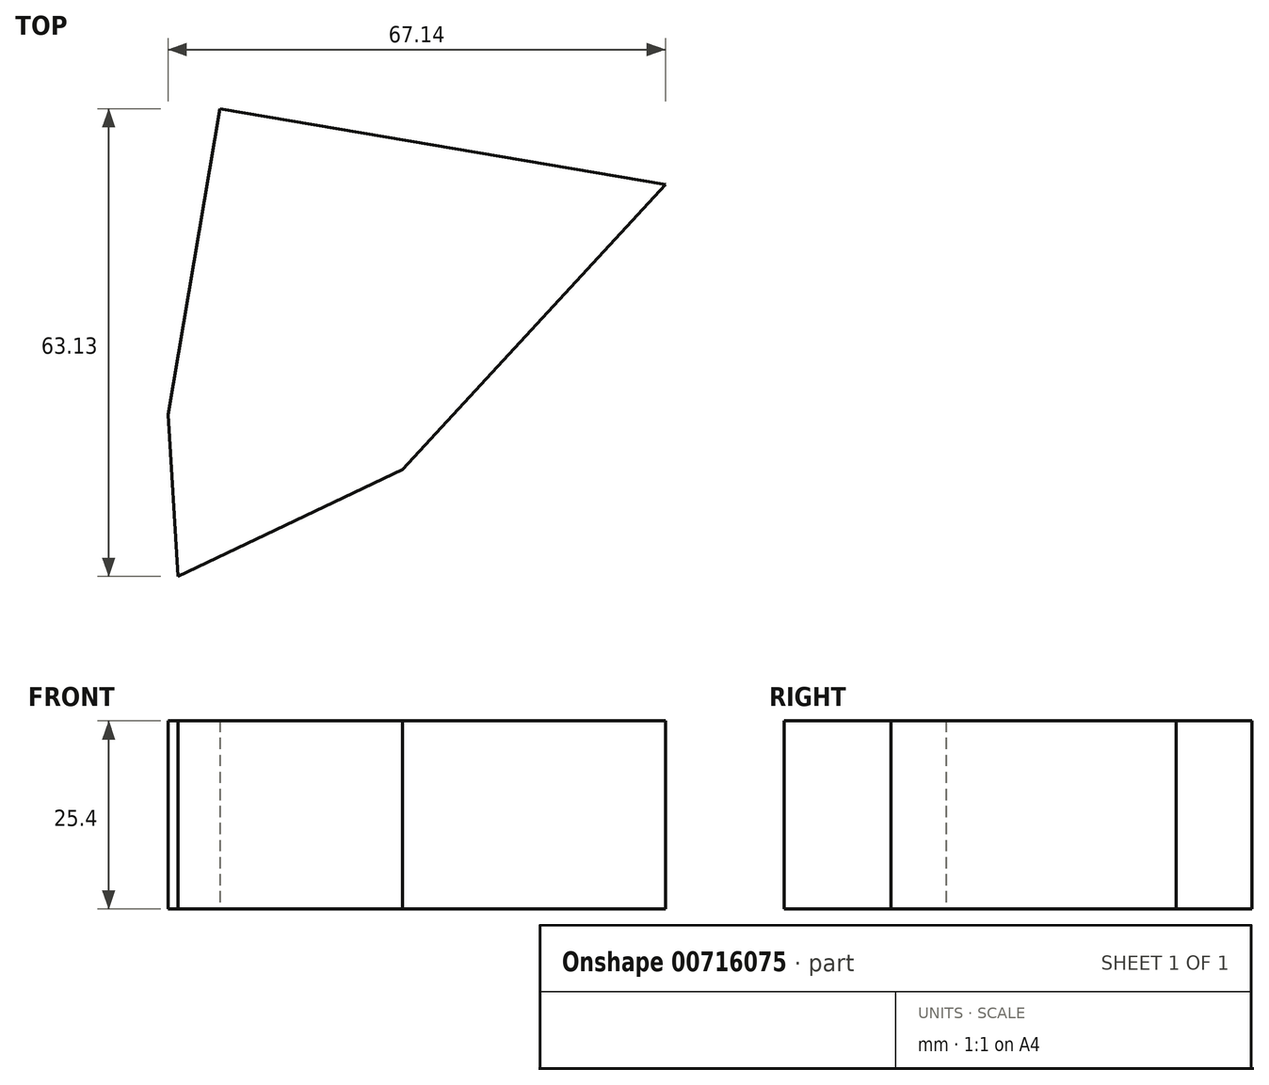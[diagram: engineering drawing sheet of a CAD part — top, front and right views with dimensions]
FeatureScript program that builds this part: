
annotation { "Feature Type Name" : "Feature", "Feature Type Description" : "" }
export const myFeature = defineFeature(function(context is Context, id is Id, definition is map)
    precondition{}
    {
        {
            var Q0;
            Q0=qCreatedBy(makeId("Top.planeOp"),FACE);
            var sketch = newSketch(context, id + "F0", { "sketchPlane" : qUnion([Q0])});
            skLineSegment(sketch, "E0", {"start": v(0.47, -0.1) * mm, "end": v(35.93, 38.4) * mm});
            skLineSegment(sketch, "E1", {"start": v(35.93, 38.4) * mm, "end": v(-24.17, 48.63) * mm});
            skLineSegment(sketch, "E2", {"start": v(-24.17, 48.63) * mm, "end": v(-31.2, 7.34) * mm});
            skLineSegment(sketch, "E3", {"start": v(-31.2, 7.34) * mm, "end": v(-29.86, -14.5) * mm});
            skLineSegment(sketch, "E4", {"start": v(-29.86, -14.5) * mm, "end": v(0.47, -0.1) * mm});
            skSolve(sketch);
        }
        {
            var Q0;
            Q0=makeQuery(id+"F0.imprint","IMPRINT",FACE,{"disambiguationData":[TD([[makeQuery(id+"F0.imprint","IMPRINT",EDGE,{"derivedFrom":sQuery(id+"F0.wireOp",EDGE,"E0")}),1.0]])]});
            extrude(context, id + "F1", {"entities" : qUnion([Q0]), "depth" : 25.4 * mm, "offsetDistance" : 25.4 * mm});
        }
    });
